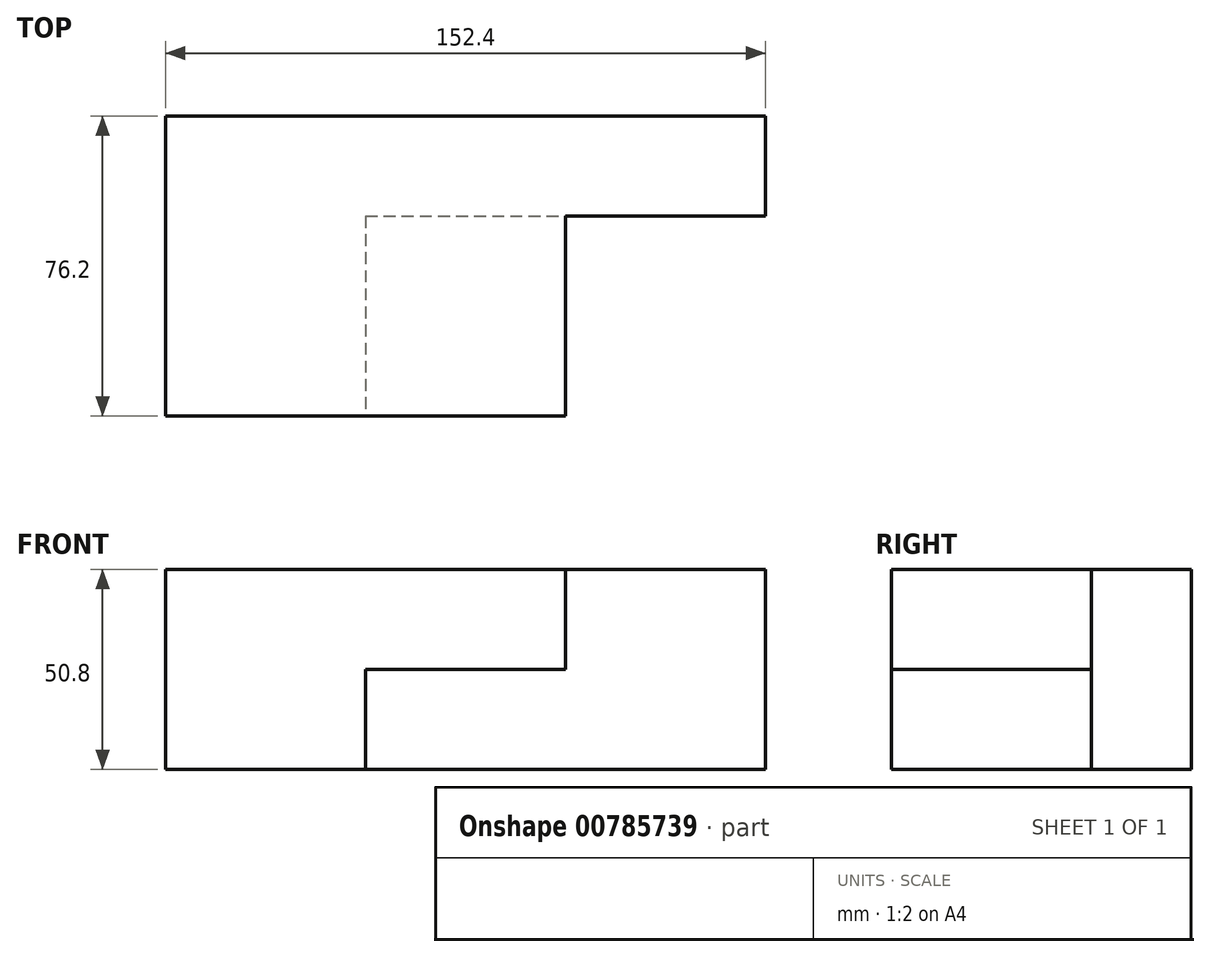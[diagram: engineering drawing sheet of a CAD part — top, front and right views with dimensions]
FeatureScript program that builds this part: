
annotation { "Feature Type Name" : "Feature", "Feature Type Description" : "" }
export const myFeature = defineFeature(function(context is Context, id is Id, definition is map)
    precondition{}
    {
        {
            var Q0;
            Q0=qCreatedBy(makeId("Front.planeOp"),FACE);
            var sketch = newSketch(context, id + "F0", { "sketchPlane" : qUnion([Q0])});
            skLineSegment(sketch, "E0", {"start": v(0, 0) * mm, "end": v(152.4, 0) * mm});
            skLineSegment(sketch, "E1", {"start": v(152.4, 0) * mm, "end": v(152.4, 50.8) * mm});
            skLineSegment(sketch, "E2", {"start": v(152.4, 50.8) * mm, "end": v(0, 50.8) * mm});
            skLineSegment(sketch, "E3", {"start": v(0, 50.8) * mm, "end": v(0, 0) * mm});
            skSolve(sketch);
        }
        {
            var Q0;
            Q0=makeQuery(id+"F0.imprint","IMPRINT",FACE,{"disambiguationData":[TD([[makeQuery(id+"F0.imprint","IMPRINT",EDGE,{"derivedFrom":sQuery(id+"F0.wireOp",EDGE,"E0")}),1.0]])]});
            extrude(context, id + "F1", {"entities" : qUnion([Q0]), "depth" : 76.2 * mm, "offsetDistance" : 25.4 * mm});
        }
        {
            var Q0;
            Q0=makeQuery(id+"F1.opExtrude","CAP_FACE",FACE,{"disambiguationData":[OSD([sQuery(id+"F0.wireOp",EDGE,"E0"),sQuery(id+"F0.wireOp",EDGE,"E1"),sQuery(id+"F0.wireOp",EDGE,"E2"),sQuery(id+"F0.wireOp",EDGE,"E3")])],"isStart":false});
            var sketch = newSketch(context, id + "F2", { "sketchPlane" : qUnion([Q0])});
            skLineSegment(sketch, "E4", {"start": v(152.4, 0) * mm, "end": v(101.6, 0) * mm});
            skLineSegment(sketch, "E5", {"start": v(101.6, 0) * mm, "end": v(101.6, 50.8) * mm});
            skLineSegment(sketch, "E6", {"start": v(101.6, 25.4) * mm, "end": v(152.4, 25.4) * mm});
            skSolve(sketch);
        }
        {
            var Q0;
            {var subQ0=sQuery(id+"F2.wireOp",EDGE,"E4");Q0=makeQuery(id+"F2.imprint","IMPRINT",FACE,{"disambiguationData":[TD([[makeQuery(id+"F2.imprint","IMPRINT",EDGE,{"derivedFrom":subQ0}),1.0]])]});}
            var Q1;
            {var subQ3=sQuery(id+"F2.wireOp",EDGE,"E6");Q1=makeQuery(id+"F2.imprint","IMPRINT",FACE,{"disambiguationData":[TD([[makeQuery(id+"F2.imprint","IMPRINT",EDGE,{"derivedFrom":subQ3}),1.0]])]});}
            extrude(context, id + "F3", {"entities" : qUnion([Q0, Q1]), "operationType" : NewBodyOperationType.REMOVE, "oppositeDirection" : true, "depth" : 50.8 * mm, "offsetDistance" : 25.4 * mm});
        }
        {
            var Q0;
            Q0=makeQuery(id+"F3.boolean.opBoolean","COPY",FACE,{"derivedFrom":makeQuery(id+"F3.opExtrude","SWEPT_FACE",FACE,{"disambiguationData":[OSD([sQuery(id+"F2.wireOp",EDGE,"E5")])]})});
            var sketch = newSketch(context, id + "F4", { "sketchPlane" : qUnion([Q0])});
            skLineSegment(sketch, "E7", {"start": v(-76.2, 0) * mm, "end": v(-76.2, 25.4) * mm});
            skLineSegment(sketch, "E8", {"start": v(-76.2, 25.4) * mm, "end": v(-25.4, 25.4) * mm});
            skSolve(sketch);
        }
        {
            var Q0;
            Q0=makeQuery(id+"F4.imprint","IMPRINT",FACE,{"disambiguationData":[TD([[makeQuery(id+"F4.imprint","IMPRINT",EDGE,{"derivedFrom":sQuery(id+"F4.wireOp",EDGE,"E7")}),-1.0]])]});
            extrude(context, id + "F5", {"entities" : qUnion([Q0]), "operationType" : NewBodyOperationType.REMOVE, "oppositeDirection" : true, "depth" : 50.8 * mm, "offsetDistance" : 25.4 * mm});
        }
    });
